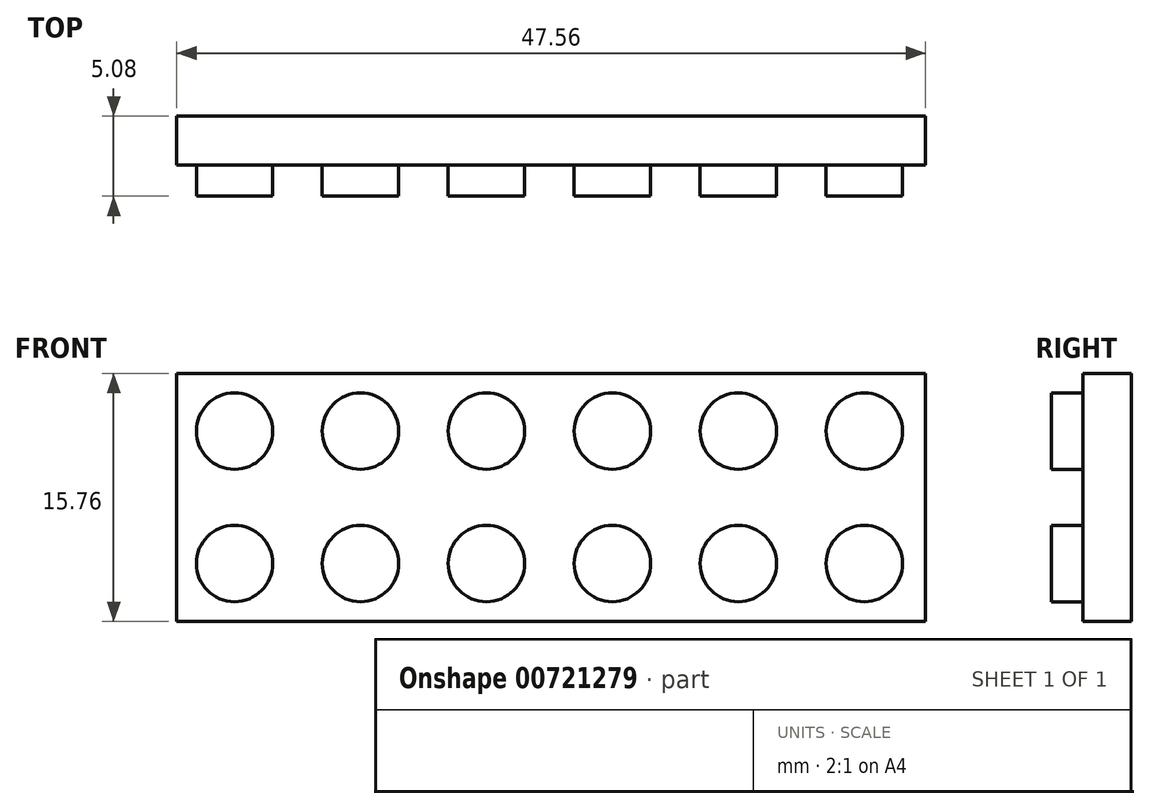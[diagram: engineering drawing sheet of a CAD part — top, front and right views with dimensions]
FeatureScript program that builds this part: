
annotation { "Feature Type Name" : "Feature", "Feature Type Description" : "" }
export const myFeature = defineFeature(function(context is Context, id is Id, definition is map)
    precondition{}
    {
        {
            var Q0;
            Q0=qCreatedBy(makeId("Front.planeOp"),FACE);
            var sketch = newSketch(context, id + "F0", { "sketchPlane" : qUnion([Q0])});
            skLineSegment(sketch, "E0.bottom", {"start": v(-42.42, 31.56) * mm, "end": v(5.14, 31.56) * mm});
            skLineSegment(sketch, "E0.top", {"start": v(-42.42, 15.8) * mm, "end": v(5.14, 15.8) * mm});
            skLineSegment(sketch, "E0.left", {"start": v(-42.42, 31.56) * mm, "end": v(-42.42, 15.8) * mm});
            skLineSegment(sketch, "E0.right", {"start": v(5.14, 31.56) * mm, "end": v(5.14, 15.8) * mm});
            skSolve(sketch);
        }
        {
            var Q0;
            Q0 = qSketchRegion(id + "F0", true);
            extrude(context, id + "F1", {"entities" : qUnion([Q0]), "depth" : 3.1 * mm, "offsetDistance" : 25 * mm});
        }
        {
            var Q0;
            Q0=makeQuery(id+"F1.opExtrude","CAP_FACE",FACE,{"disambiguationData":[OSD([sQuery(id+"F0.wireOp",EDGE,"E0.bottom"),sQuery(id+"F0.wireOp",EDGE,"E0.top"),sQuery(id+"F0.wireOp",EDGE,"E0.left"),sQuery(id+"F0.wireOp",EDGE,"E0.right")])],"isStart":false});
            var sketch = newSketch(context, id + "F2", { "sketchPlane" : qUnion([Q0])});
            skCircle(sketch, "E1", {"center": v(-38.75, 19.47) * mm, "radius": 2.43 * mm});
            skCircle(sketch, "E2", {"center": v(-38.75, 27.88) * mm, "radius": 2.42 * mm});
            skCircle(sketch, "E3", {"center": v(-30.75, 27.88) * mm, "radius": 2.43 * mm});
            skCircle(sketch, "E4", {"center": v(-30.75, 19.47) * mm, "radius": 2.43 * mm});
            skCircle(sketch, "E5", {"center": v(-22.75, 27.88) * mm, "radius": 2.43 * mm});
            skCircle(sketch, "E6", {"center": v(-22.75, 19.47) * mm, "radius": 2.43 * mm});
            skCircle(sketch, "E7", {"center": v(-14.75, 19.47) * mm, "radius": 2.43 * mm});
            skCircle(sketch, "E8", {"center": v(-6.75, 19.47) * mm, "radius": 2.43 * mm});
            skCircle(sketch, "E9", {"center": v(1.25, 19.47) * mm, "radius": 2.43 * mm});
            skCircle(sketch, "E10", {"center": v(-14.75, 27.88) * mm, "radius": 2.43 * mm});
            skCircle(sketch, "E11", {"center": v(-6.75, 27.88) * mm, "radius": 2.43 * mm});
            skCircle(sketch, "E12", {"center": v(1.25, 27.88) * mm, "radius": 2.43 * mm});
            skLineSegment(sketch, "E13", {"start": v(-42.42, 31.56) * mm, "end": v(5.14, 31.56) * mm});
            skPoint(sketch, "E14.start.orphan", {"position": v(-20.32, 27.88) * mm});
            skPoint(sketch, "E15.start.orphan", {"position": v(-28.32, 27.88) * mm});
            skPoint(sketch, "E16.start.orphan", {"position": v(-28.32, 19.47) * mm});
            skPoint(sketch, "E17.start.orphan", {"position": v(-20.32, 19.47) * mm});
            skPoint(sketch, "E18.start.orphan", {"position": v(-12.32, 19.47) * mm});
            skPoint(sketch, "E19.start.orphan", {"position": v(-4.32, 19.47) * mm});
            skPoint(sketch, "E20.start.orphan", {"position": v(-4.32, 27.88) * mm});
            skPoint(sketch, "E21.start.orphan", {"position": v(-12.32, 27.88) * mm});
            skPoint(sketch, "E22.start.orphan", {"position": v(-38.75, 30.3) * mm});
            skPoint(sketch, "E23.start.orphan", {"position": v(-41.17, 27.88) * mm});
            skPoint(sketch, "E24.start.orphan", {"position": v(-36.32, 27.88) * mm});
            skPoint(sketch, "E25.start.orphan", {"position": v(-36.32, 19.47) * mm});
            skPoint(sketch, "E26.start.orphan", {"position": v(-38.75, 15.8) * mm});
            skPoint(sketch, "E27.start.orphan", {"position": v(-41.17, 19.47) * mm});
            skSolve(sketch);
        }
        {
            var Q0;
            Q0 = qSketchRegion(id + "F2", true);
            extrude(context, id + "F3", {"entities" : qUnion([Q0]), "operationType" : NewBodyOperationType.ADD, "depth" : 1.98 * mm, "offsetDistance" : 25 * mm});
        }
    });
